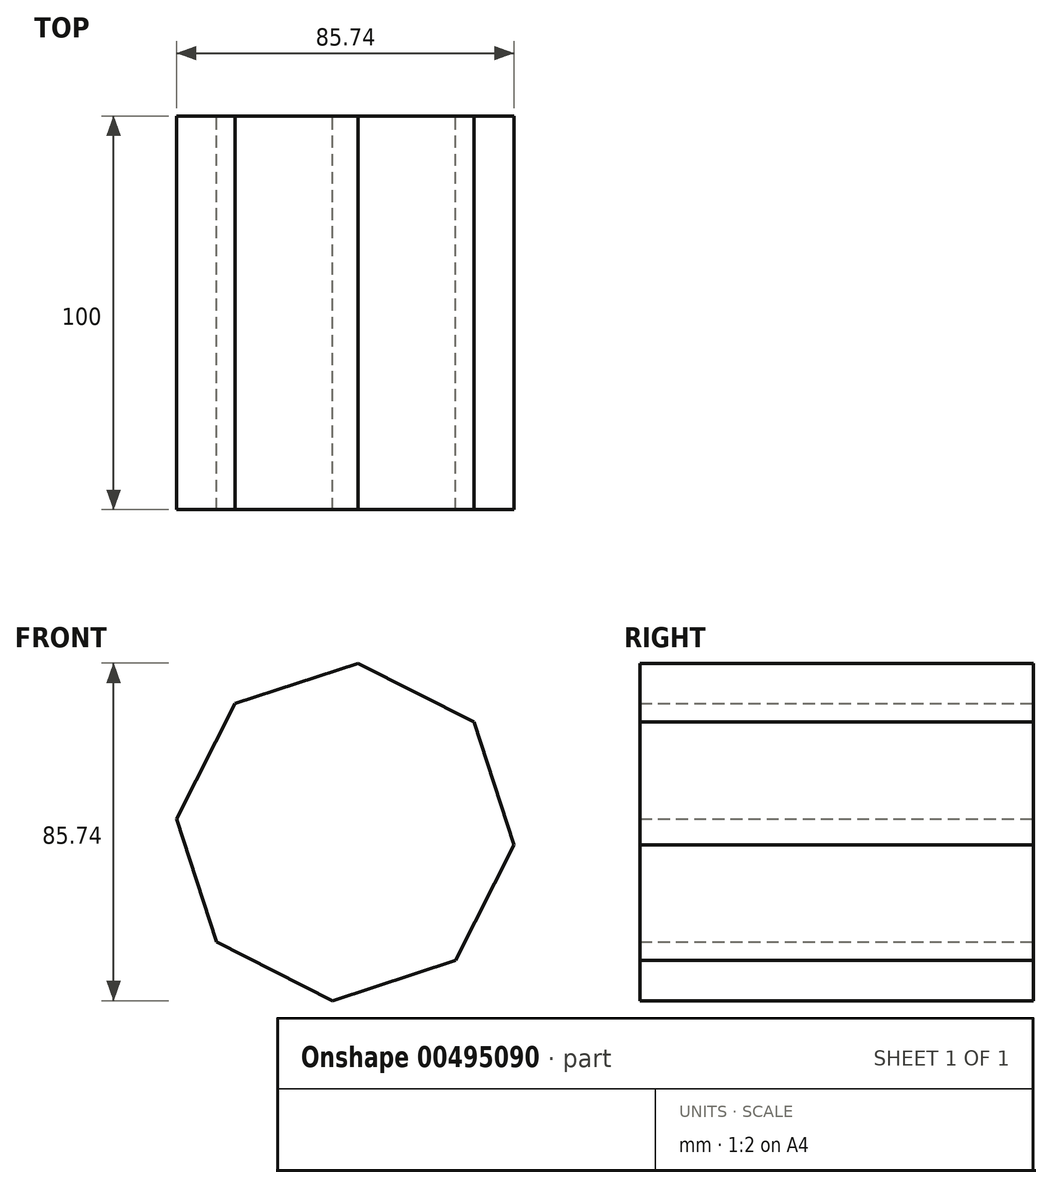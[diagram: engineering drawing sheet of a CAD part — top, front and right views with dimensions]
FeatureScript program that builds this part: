
annotation { "Feature Type Name" : "Feature", "Feature Type Description" : "" }
export const myFeature = defineFeature(function(context is Context, id is Id, definition is map)
    precondition{}
    {
        {
            var Q0;
            Q0=qCreatedBy(makeId("Front.planeOp"),FACE);
            var sketch = newSketch(context, id + "F0", { "sketchPlane" : qUnion([Q0])});
            skCircle(sketch, "E0.cCircle", {"center": v(-0.67, -0.75) * mm, "radius": 43 * mm, "construction": true});
            skLineSegment(sketch, "E0.0", {"start": v(27.3, -33.4) * mm, "end": v(-3.97, -43.62) * mm});
            skLineSegment(sketch, "E0.1", {"start": v(-3.97, -43.62) * mm, "end": v(-33.32, -28.73) * mm});
            skLineSegment(sketch, "E0.2", {"start": v(-33.32, -28.73) * mm, "end": v(-43.54, 2.55) * mm});
            skLineSegment(sketch, "E0.3", {"start": v(-43.54, 2.55) * mm, "end": v(-28.66, 31.9) * mm});
            skLineSegment(sketch, "E0.4", {"start": v(-28.66, 31.9) * mm, "end": v(2.62, 42.12) * mm});
            skLineSegment(sketch, "E0.5", {"start": v(2.62, 42.12) * mm, "end": v(31.97, 27.23) * mm});
            skLineSegment(sketch, "E0.6", {"start": v(31.97, 27.23) * mm, "end": v(42.2, -4.05) * mm});
            skLineSegment(sketch, "E0.7", {"start": v(42.2, -4.05) * mm, "end": v(27.3, -33.4) * mm});
            skSolve(sketch);
        }
        {
            var Q0;
            Q0 = qSketchRegion(id + "F0", true);
            extrude(context, id + "F1", {"entities" : qUnion([Q0]), "depth" : 100 * mm});
        }
    });
